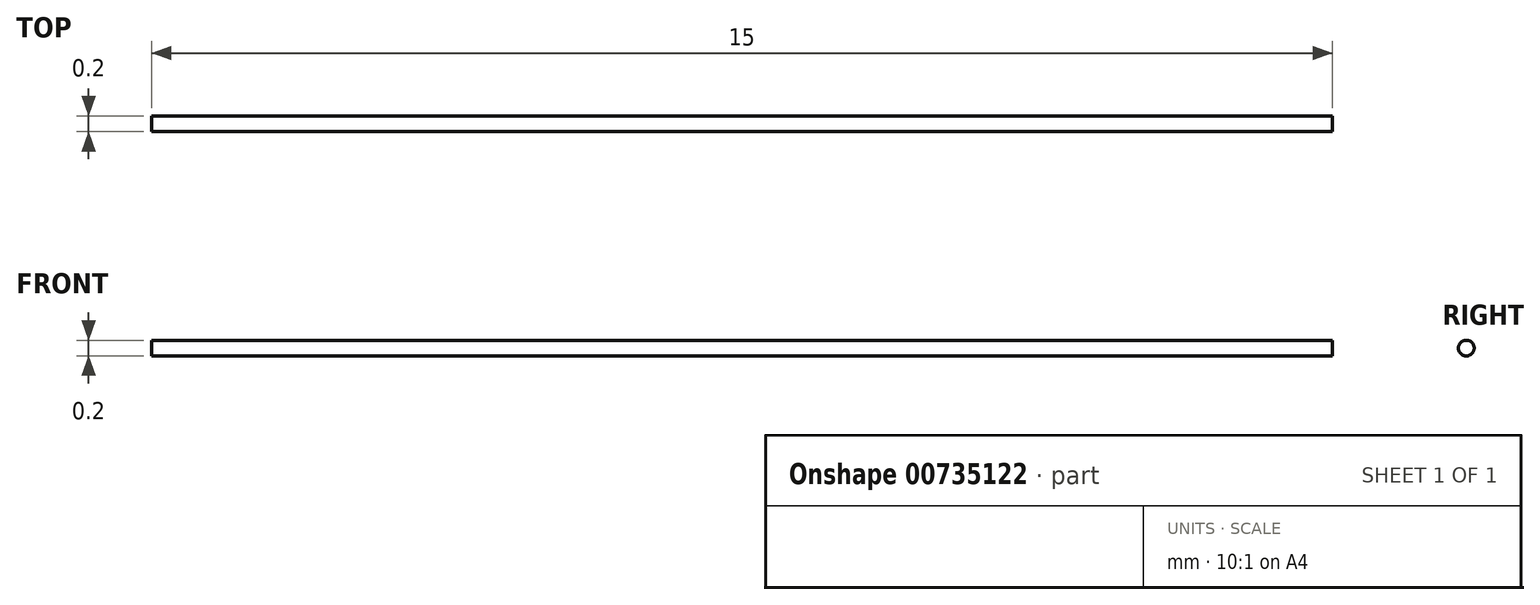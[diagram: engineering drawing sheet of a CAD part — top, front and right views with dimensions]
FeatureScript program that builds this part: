
annotation { "Feature Type Name" : "Feature", "Feature Type Description" : "" }
export const myFeature = defineFeature(function(context is Context, id is Id, definition is map)
    precondition{}
    {
        {
            var Q0;
            Q0=qCreatedBy(makeId("Right.planeOp"),FACE);
            var sketch = newSketch(context, id + "F0", { "sketchPlane" : qUnion([Q0])});
            skCircle(sketch, "E0", {"center": v(0, 0) * mm, "radius": 0.1 * mm});
            skLineSegment(sketch, "E1", {"start": v(0.1, 0) * mm, "end": v(-0.1, 0) * mm, "construction": true});
            skSolve(sketch);
        }
        {
            var Q0;
            Q0 = qSketchRegion(id + "F0", true);
            extrude(context, id + "F1", {"entities" : qUnion([Q0]), "depth" : 15 * mm, "offsetDistance" : 25 * mm});
        }
    });
